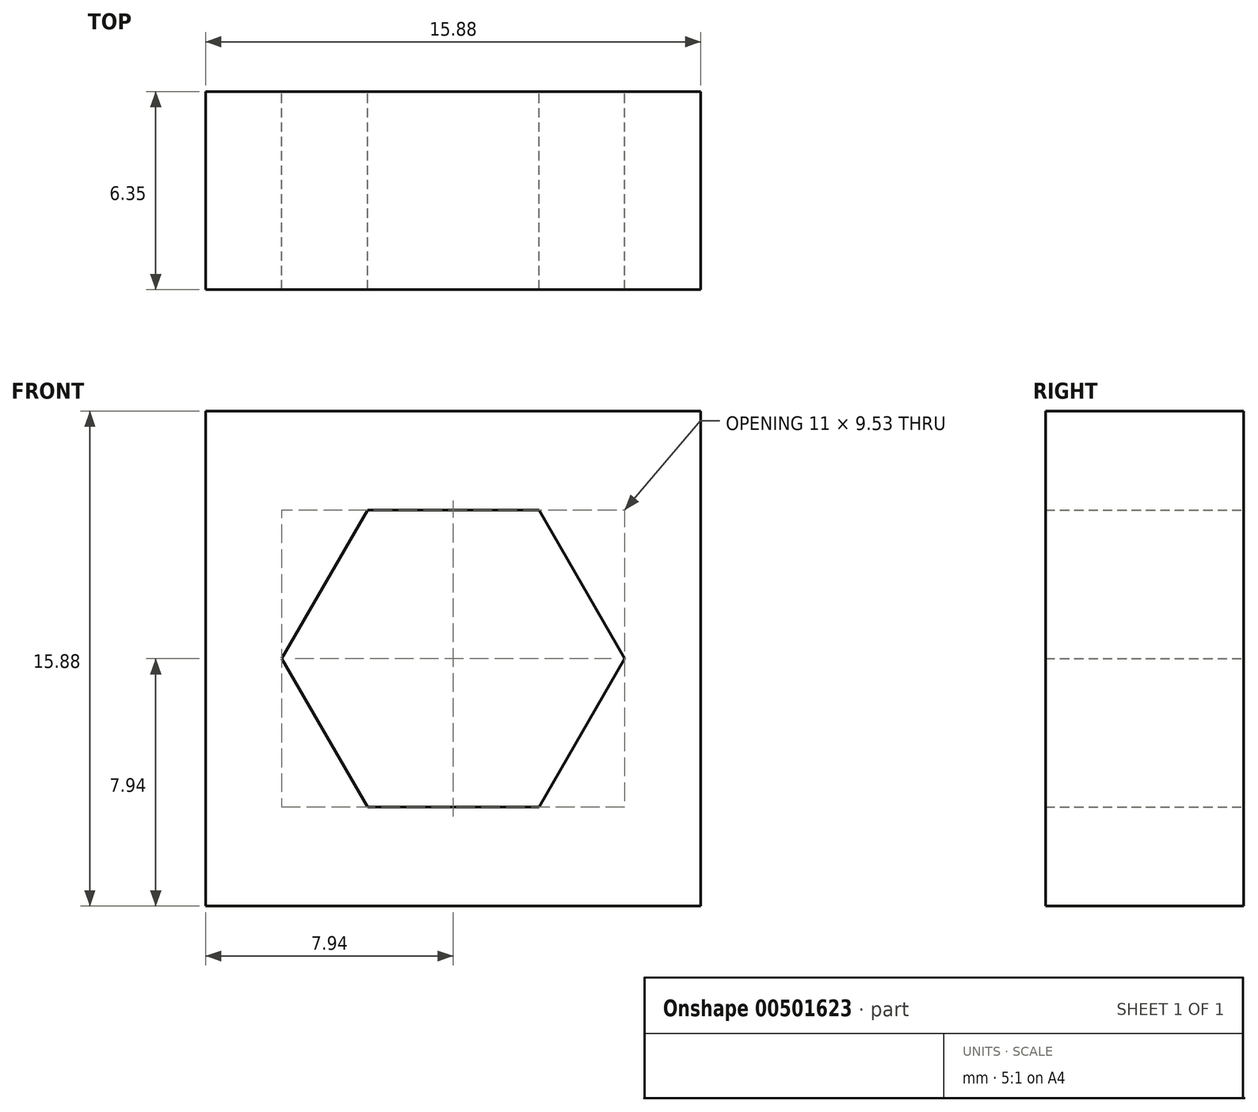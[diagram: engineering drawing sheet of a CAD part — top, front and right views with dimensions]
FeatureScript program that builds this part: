
annotation { "Feature Type Name" : "Feature", "Feature Type Description" : "" }
export const myFeature = defineFeature(function(context is Context, id is Id, definition is map)
    precondition{}
    {
        {
            var Q0;
            Q0=qCreatedBy(makeId("Front.planeOp"),FACE);
            var sketch = newSketch(context, id + "F0", { "sketchPlane" : qUnion([Q0])});
            skLineSegment(sketch, "E0.bottom", {"start": v(-7.94, 7.94) * mm, "end": v(7.94, 7.94) * mm});
            skLineSegment(sketch, "E0.top", {"start": v(-7.94, -7.94) * mm, "end": v(7.94, -7.94) * mm});
            skLineSegment(sketch, "E0.left", {"start": v(-7.94, 7.94) * mm, "end": v(-7.94, -7.94) * mm});
            skLineSegment(sketch, "E0.right", {"start": v(7.94, 7.94) * mm, "end": v(7.94, -7.94) * mm});
            skPoint(sketch, "E0.middle", {"position": v(0, 0) * mm});
            skCircle(sketch, "E1.cCircle", {"center": v(0, 0) * mm, "radius": 4.76 * mm, "construction": true});
            skLineSegment(sketch, "E1.0", {"start": v(-2.75, 4.76) * mm, "end": v(2.75, 4.76) * mm});
            skLineSegment(sketch, "E1.1", {"start": v(2.75, 4.76) * mm, "end": v(5.5, 0) * mm});
            skLineSegment(sketch, "E1.2", {"start": v(5.5, 0) * mm, "end": v(2.75, -4.76) * mm});
            skLineSegment(sketch, "E1.3", {"start": v(2.75, -4.76) * mm, "end": v(-2.75, -4.76) * mm});
            skLineSegment(sketch, "E1.4", {"start": v(-2.75, -4.76) * mm, "end": v(-5.5, 0) * mm});
            skLineSegment(sketch, "E1.5", {"start": v(-5.5, 0) * mm, "end": v(-2.75, 4.76) * mm});
            skPoint(sketch, "E1.0.midPoint", {"position": v(0, 4.76) * mm});
            skSolve(sketch);
        }
        {
            var Q0;
            Q0=qSketchRegion(id+"F0",true);
            extrude(context, id + "F1", {"entities" : qUnion([Q0]), "depth" : 6.35 * mm});
        }
    });
